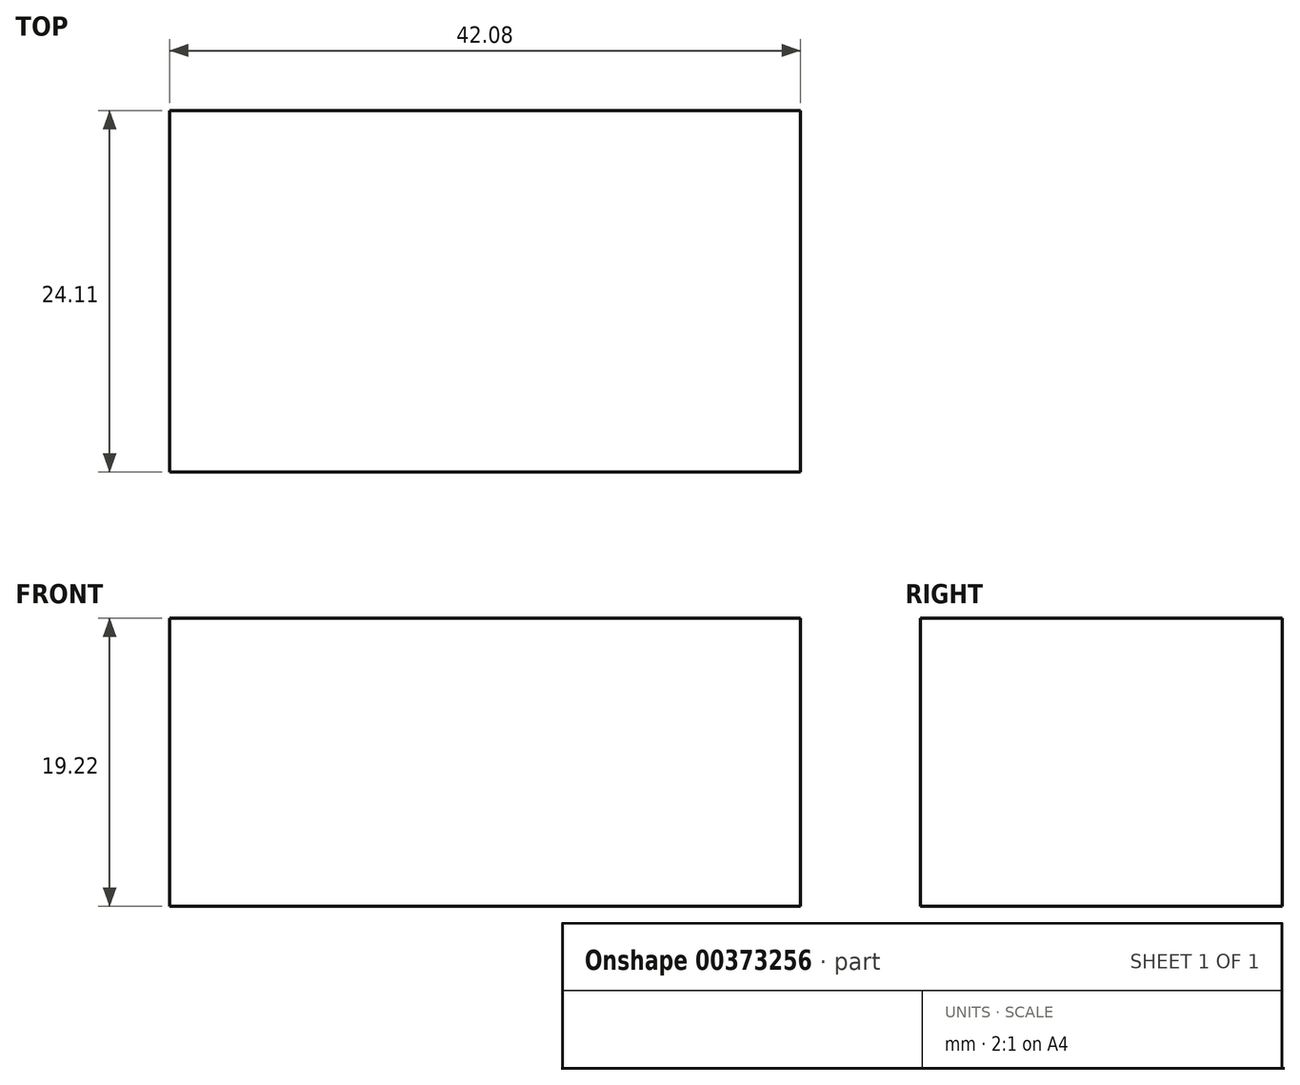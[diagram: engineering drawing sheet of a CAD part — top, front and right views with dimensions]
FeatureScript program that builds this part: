
annotation { "Feature Type Name" : "Feature", "Feature Type Description" : "" }
export const myFeature = defineFeature(function(context is Context, id is Id, definition is map)
    precondition{}
    {
        {
            var Q0;
            Q0=qCreatedBy(makeId("Front.planeOp"),FACE);
            var sketch = newSketch(context, id + "F0", { "sketchPlane" : qUnion([Q0])});
            skLineSegment(sketch, "E0", {"start": v(-19.32, 19.22) * mm, "end": v(22.76, 19.22) * mm});
            skLineSegment(sketch, "E1", {"start": v(22.76, 19.22) * mm, "end": v(22.76, 0) * mm});
            skLineSegment(sketch, "E2", {"start": v(22.76, 0) * mm, "end": v(-19.32, 0) * mm});
            skLineSegment(sketch, "E3", {"start": v(-19.32, 0) * mm, "end": v(-19.32, 19.22) * mm});
            skSolve(sketch);
        }
        {
            var Q0;
            Q0=makeQuery(id+"F0.imprint","IMPRINT",FACE,{"disambiguationData":[TD([[makeQuery(id+"F0.imprint","IMPRINT",EDGE,{"derivedFrom":sQuery(id+"F0.wireOp",EDGE,"E0")}),-1.0]])]});
            extrude(context, id + "F1", {"entities" : qUnion([Q0]), "depth" : 24.1 * mm});
        }
    });
